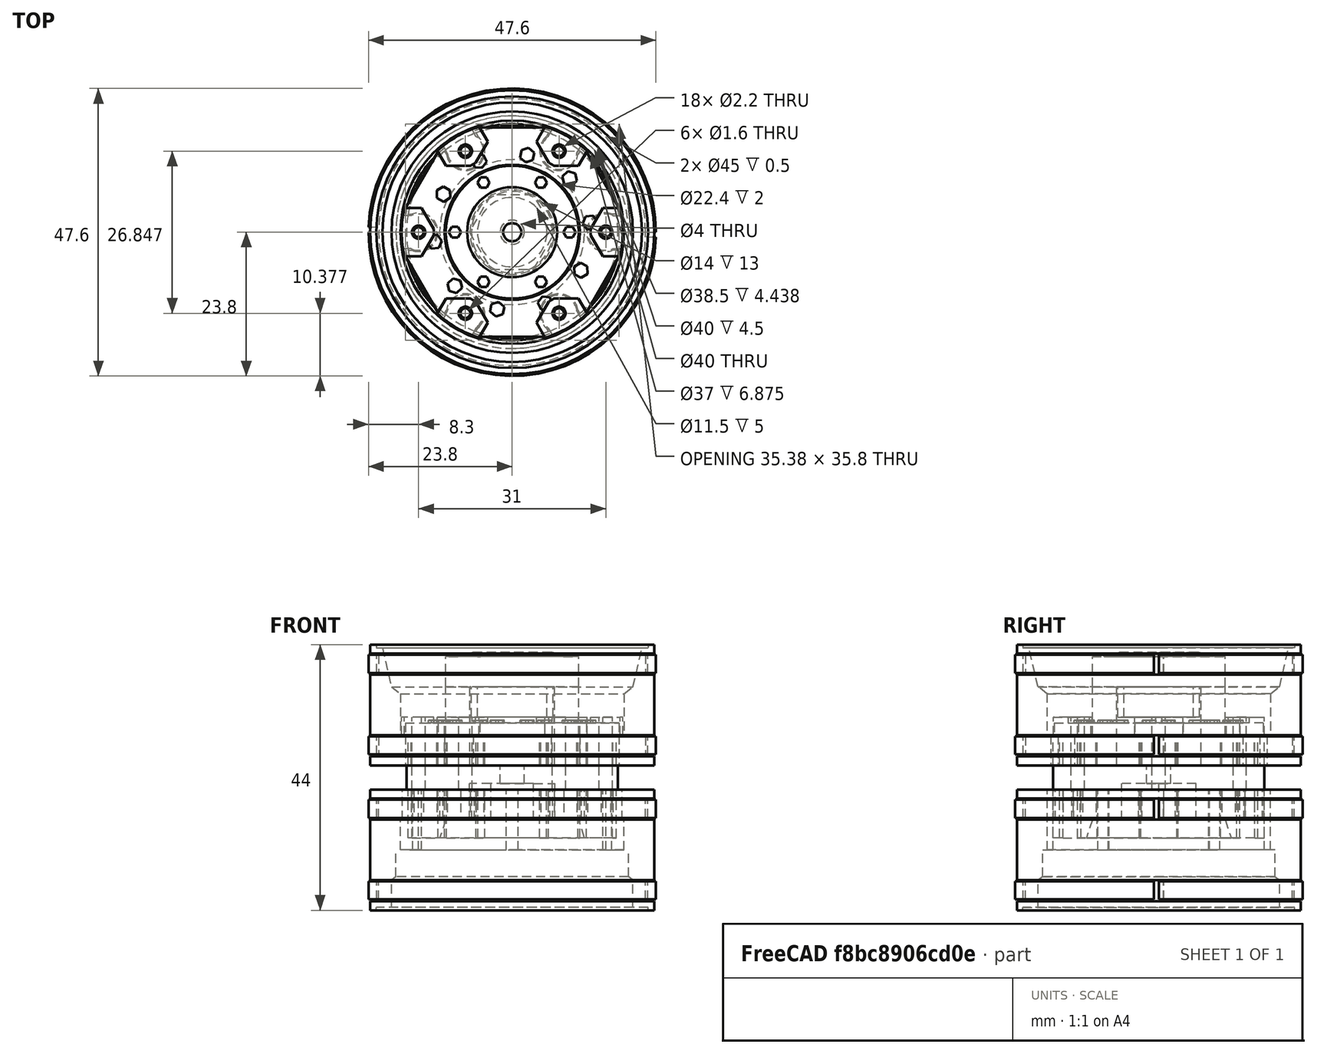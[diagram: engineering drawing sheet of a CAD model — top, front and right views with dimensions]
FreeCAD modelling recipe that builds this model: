
FCSTD DOCUMENT  (FreeCAD 0.18.4R)
Label: trilex_rear
License: All rights reserved
LicenseURL: http://en.wikipedia.org/wiki/All_rights_reserved
objects: Part::Cylinder×79, Part::MultiFuse×62, Part::Cut×43, Part::Box×17, Part::Feature×13, Part::Extrusion×5, Part::RegularPolygon×4, Part::Cone×3, Part::Fillet×2, Part::Chamfer×2
note: 230 computed .brp shape members not serialized (recipe doc carries the construction recipe); baked Part::Feature solids carry a one-line shape summary decoded from their .brp

FEATURE [Part::Cylinder] Cylinder
  Angle = 360
  AttacherType = Attacher::AttachEngine3D
  Height = 20
  Radius = 23.5
FEATURE [Part::Cylinder] Cylinder002
  Angle = 360
  AttacherType = Attacher::AttachEngine3D
  Height = 17
  Radius = 22.1
FEATURE [Part::Cylinder] Cylinder001
  Angle = 360
  AttacherType = Attacher::AttachEngine3D
  Height = 17
  Radius = 23.5
FEATURE [Part::Cut] Cut
  Base = -> Cylinder001
  Placement = pos=(0,0,1.5) rot=(0,0,1;0rad)
  Refine = true
  Tool = -> Cylinder002
FEATURE [Part::Cut] Cut001
  Base = -> Cylinder
  Refine = true
  Tool = -> Cut
FEATURE [Part::Cylinder] Cylinder003
  Angle = 360
  AttacherType = Attacher::AttachEngine3D
  Height = 17
  Radius = 22
FEATURE [Part::Cylinder] Cylinder004
  Angle = 360
  AttacherType = Attacher::AttachEngine3D
  Height = 10
  Placement = pos=(0,0,0.5) rot=(0,0,1;0rad)
  Radius = 23.5
FEATURE [Part::Cut] Cut002
  Base = -> Cylinder004
  Placement = pos=(0,0,4.5) rot=(0,0,1;0rad)
  Refine = true
  Tool = -> Cylinder003
FEATURE [Part::Cylinder] Cylinder006
  Angle = 360
  AttacherType = Attacher::AttachEngine3D
  Height = 20
  Radius = 18.5
FEATURE [Part::Cylinder] Cylinder007
  Angle = 360
  AttacherType = Attacher::AttachEngine3D
  Height = 5
  Placement = pos=(0,0,5) rot=(0,0,1;0rad)
  Radius = 19.25
FEATURE [Part::Cylinder] Cylinder018
  Angle = 360
  AttacherType = Attacher::AttachEngine3D
  Height = 0.5
  Radius = 22.5
FEATURE [Part::Cylinder] Cylinder070
  Angle = 360
  AttacherType = Attacher::AttachEngine3D
  Height = 5
  Radius = 20
FEATURE [Part::Cylinder] Cylinder071
  Angle = 360
  AttacherType = Attacher::AttachEngine3D
  Height = 10
  Placement = pos=(18.5,0,5) rot=(0,0,1;0rad)
  Radius = 1
FEATURE [Part::Cylinder] Cylinder072
  Angle = 360
  AttacherType = Attacher::AttachEngine3D
  Height = 10
  Placement = pos=(9.25,16.0215,5) rot=(0,0,1;1.0472rad)
  Radius = 1
FEATURE [Part::Cylinder] Cylinder073
  Angle = 360
  AttacherType = Attacher::AttachEngine3D
  Height = 10
  Placement = pos=(-9.25,16.0215,5) rot=(0,0,1;2.0944rad)
  Radius = 1
FEATURE [Part::Cylinder] Cylinder074
  Angle = 360
  AttacherType = Attacher::AttachEngine3D
  Height = 10
  Placement = pos=(-18.5,2e-15,5) rot=(0,0,1;3.14159rad)
  Radius = 1
FEATURE [Part::Cylinder] Cylinder075
  Angle = 360
  AttacherType = Attacher::AttachEngine3D
  Height = 10
  Placement = pos=(-9.25,-16.0215,5) rot=(0,0,1;4.18879rad)
  Radius = 1
FEATURE [Part::Cylinder] Cylinder076
  Angle = 360
  AttacherType = Attacher::AttachEngine3D
  Height = 10
  Placement = pos=(9.25,-16.0215,5) rot=(0,0,-1;1.0472rad)
  Radius = 1
FEATURE [Part::MultiFuse] Fusion030  label="rim-enforcement"
  Placement = pos=(0,0,-39) rot=(0,0,1;0.523599rad)
  Refine = true
  Shapes = -> [Cylinder071,Cylinder073,Cylinder075,Cylinder072,Cylinder074,Cylinder076]
FEATURE [Part::MultiFuse] Fusion
  Refine = true
  Shapes = -> [Cut002,Cut001]
FEATURE [Part::Cut] Cut031
  Base = -> Fusion
  Refine = true
  Tool = -> Cylinder006
FEATURE [Part::Cylinder] Cylinder078
  Angle = 178
  AttacherType = Attacher::AttachEngine3D
  Height = 3
  Placement = pos=(0,0,1.8) rot=(0,0,1;0rad)
  Radius = 23.8
FEATURE [Part::Cylinder] Cylinder079
  Angle = 360
  AttacherType = Attacher::AttachEngine3D
  Height = 17
  Radius = 22.45
FEATURE [Part::Cut] Cut035
  Base = -> Cylinder078
  Refine = true
  Tool = -> Cylinder079
FEATURE [Part::Cylinder] Cylinder080
  Angle = 178
  AttacherType = Attacher::AttachEngine3D
  Height = 3
  Placement = pos=(0,0,1.8) rot=(0,0,1;0rad)
  Radius = 23.8
FEATURE [Part::Cylinder] Cylinder081
  Angle = 360
  AttacherType = Attacher::AttachEngine3D
  Height = 17
  Radius = 22.45
FEATURE [Part::Cut] Cut036
  Base = -> Cylinder080
  Placement = pos=(0,0,0) rot=(0,0,1;3.14159rad)
  Refine = true
  Tool = -> Cylinder081
FEATURE [Part::MultiFuse] Fusion032
  Placement = pos=(0,0,13.5) rot=(0,0,1;0rad)
  Refine = true
  Shapes = -> [Cut035,Cut036]
FEATURE [Part::Cut] Cut037
  Base = -> Cylinder080
  Placement = pos=(0,0,0) rot=(0,0,1;3.14159rad)
  Refine = true
  Tool = -> Cylinder081
FEATURE [Part::Cut] Cut038
  Base = -> Cylinder078
  Refine = true
  Tool = -> Cylinder079
FEATURE [Part::MultiFuse] Fusion033
  Refine = true
  Shapes = -> [Cut038,Cut037]
FEATURE [Part::MultiFuse] Fusion034  label="trilex-rear-rim-inner-support"
  Placement = pos=(0,0,-44) rot=(0,0,1;0rad)
  Refine = true
  Shapes = -> [Fusion032,Fusion033]
FEATURE [Part::Cone] Cone
  Angle = 360
  AttacherType = Attacher::AttachEngine3D
  Height = 6
  Placement = pos=(0,0,5) rot=(0,0,1;0rad)
  Radius1 = 20
  Radius2 = 12
FEATURE [Part::Cut] Cut057
  Base = -> Cut031
  Refine = true
  Tool = -> Cylinder070
FEATURE [Part::Cut] Cut058
  Base = -> Cut057
  Refine = true
  Tool = -> Cylinder018
FEATURE [Part::Cut] Cut059
  Base = -> Cut058
  Refine = true
  Tool = -> Cone
FEATURE [Part::Cut] Cut060  label="rim-inner"
  Base = -> Cut059
  Placement = pos=(0,0,44) rot=(0,1,0;3.14159rad)
  Refine = true
  Tool = -> Cylinder007
FEATURE [Part::Cylinder] Cylinder098
  Angle = 360
  AttacherType = Attacher::AttachEngine3D
  Height = 5
  Placement = pos=(15.5,0,15) rot=(0,0,1;0rad)
  Radius = 0.8
FEATURE [Part::Cylinder] Cylinder100
  Angle = 360
  AttacherType = Attacher::AttachEngine3D
  Height = 5
  Placement = pos=(15.5,0,15) rot=(0,0,1;0rad)
  Radius = 3
FEATURE [Part::Box] Box012  label="Cube012"
  AttacherType = Attacher::AttachEngine3D
  Height = 5
  Length = 0.75
  Placement = pos=(18.2,-4,15) rot=(0,0,1;0rad)
  Width = 8
FEATURE [Part::Box] Box013  label="Cube013"
  AttacherType = Attacher::AttachEngine3D
  Height = 5
  Length = 2
  Placement = pos=(16.5,-2.75,15) rot=(0,0,1;0rad)
  Width = 5.5
FEATURE [Part::MultiFuse] Fusion042
  Refine = true
  Shapes = -> [Cylinder100,Box013,Box012]
FEATURE [Part::Cut] Cut063
  Base = -> Fusion042
  Placement = pos=(0,0,9) rot=(0,0,1;1.0472rad)
  Refine = true
  Tool = -> Cylinder098
FEATURE [Part::Cylinder] Cylinder101
  Angle = 360
  AttacherType = Attacher::AttachEngine3D
  Height = 5
  Placement = pos=(15.5,0,15) rot=(0,0,1;0rad)
  Radius = 0.8
FEATURE [Part::MultiFuse] Fusion043
  Refine = true
  Shapes = -> [Cylinder100,Box013,Box012]
FEATURE [Part::Cut] Cut064
  Base = -> Fusion043
  Placement = pos=(0,0,9) rot=(0,0,1;2.0944rad)
  Refine = true
  Tool = -> Cylinder101
FEATURE [Part::Cylinder] Cylinder102
  Angle = 360
  AttacherType = Attacher::AttachEngine3D
  Height = 5
  Placement = pos=(15.5,0,15) rot=(0,0,1;0rad)
  Radius = 0.8
FEATURE [Part::MultiFuse] Fusion044
  Refine = true
  Shapes = -> [Cylinder100,Box013,Box012]
FEATURE [Part::Cut] Cut065
  Base = -> Fusion044
  Placement = pos=(0,0,9) rot=(0,0,1;3.14159rad)
  Refine = true
  Tool = -> Cylinder102
FEATURE [Part::Cylinder] Cylinder103
  Angle = 360
  AttacherType = Attacher::AttachEngine3D
  Height = 5
  Placement = pos=(15.5,0,15) rot=(0,0,1;0rad)
  Radius = 0.8
FEATURE [Part::MultiFuse] Fusion045
  Refine = true
  Shapes = -> [Cylinder100,Box013,Box012]
FEATURE [Part::Cut] Cut066
  Base = -> Fusion045
  Placement = pos=(0,0,9) rot=(0,0,1;4.18879rad)
  Refine = true
  Tool = -> Cylinder103
FEATURE [Part::Cylinder] Cylinder104
  Angle = 360
  AttacherType = Attacher::AttachEngine3D
  Height = 5
  Placement = pos=(15.5,0,15) rot=(0,0,1;0rad)
  Radius = 0.8
FEATURE [Part::MultiFuse] Fusion046
  Refine = true
  Shapes = -> [Cylinder100,Box013,Box012]
FEATURE [Part::Cut] Cut067
  Base = -> Fusion046
  Placement = pos=(0,0,9) rot=(0,0,-1;1.0472rad)
  Refine = true
  Tool = -> Cylinder104
FEATURE [Part::Cylinder] Cylinder106
  Angle = 360
  AttacherType = Attacher::AttachEngine3D
  Height = 5
  Placement = pos=(15.5,0,15) rot=(0,0,1;0rad)
  Radius = 0.8
FEATURE [Part::MultiFuse] Fusion048
  Refine = true
  Shapes = -> [Cylinder100,Box013,Box012]
FEATURE [Part::Cut] Cut069
  Base = -> Fusion048
  Placement = pos=(0,0,9) rot=(0,0,1;0rad)
  Refine = true
  Tool = -> Cylinder106
FEATURE [Part::MultiFuse] Fusion049
  Refine = true
  Shapes = -> [Cut063,Cut064,Cut067,Cut065,Cut069,Cut066]
FEATURE [Part::MultiFuse] Fusion050  label="rim-inner-rear_"
  Placement = pos=(0,0,0) rot=(0,1,0;3.14159rad)
  Refine = true
  Shapes = -> [Cut060,Fusion049]
FEATURE [Part::Cylinder] Cylinder109
  Angle = 360
  AttacherType = Attacher::AttachEngine3D
  Height = 2
  Placement = pos=(0,0,-6) rot=(0,0,1;0rad)
  Radius = 7.5
FEATURE [Part::Fillet] Fillet059
  Base = -> Cylinder109
  Edges = 1 edges r=1: [Edge1]
  Placement = pos=(0,0,-6) rot=(0,0,1;0rad)
FEATURE [Part::Cylinder] Cylinder112
  Angle = 360
  AttacherType = Attacher::AttachEngine3D
  Height = 0.3
  Placement = pos=(0,0,-10.3) rot=(0,0,1;0rad)
  Radius = 1.5
FEATURE [Part::Cut] Cut072
  Base = -> Fillet059
  Refine = true
  Tool = -> Cylinder112
FEATURE [Part::Fillet] Fillet062
  Base = -> Cut072
  Edges = 1 edges r=0.29: [Edge6]
  Placement = pos=(0,0,8.7) rot=(0,0,1;0rad)
FEATURE [Part::Cylinder] Cylinder118
  Angle = 360
  AttacherType = Attacher::AttachEngine3D
  Height = 17
  Placement = pos=(0,0,-32) rot=(0,0,1;0rad)
  Radius = 17.5
FEATURE [Part::Cylinder] Cylinder119
  Angle = 360
  AttacherType = Attacher::AttachEngine3D
  Height = 8
  Placement = pos=(15.5,0,-29.5) rot=(0,0,1;0rad)
  Radius = 3.2
FEATURE [Part::Box] Box016  label="Cube016"
  AttacherType = Attacher::AttachEngine3D
  Height = 8
  Length = 3
  Placement = pos=(16,-3,-29.5) rot=(0,0,1;0rad)
  Width = 6
FEATURE [Part::MultiFuse] Fusion061
  Placement = pos=(0,0,0) rot=(0,0,1;1.0472rad)
  Refine = true
  Shapes = -> [Cylinder119,Box016]
FEATURE [Part::Cylinder] Cylinder120
  Angle = 360
  AttacherType = Attacher::AttachEngine3D
  Height = 8
  Placement = pos=(15.5,0,-29.5) rot=(0,0,1;0rad)
  Radius = 3.2
FEATURE [Part::Box] Box017  label="Cube017"
  AttacherType = Attacher::AttachEngine3D
  Height = 8
  Length = 3
  Placement = pos=(16,-3,-29.5) rot=(0,0,1;0rad)
  Width = 6
FEATURE [Part::MultiFuse] Fusion062
  Placement = pos=(0,0,0) rot=(0,0,1;2.0944rad)
  Refine = true
  Shapes = -> [Cylinder120,Box017]
FEATURE [Part::Cylinder] Cylinder121
  Angle = 360
  AttacherType = Attacher::AttachEngine3D
  Height = 8
  Placement = pos=(15.5,0,-29.5) rot=(0,0,1;0rad)
  Radius = 3.2
FEATURE [Part::Box] Box018  label="Cube018"
  AttacherType = Attacher::AttachEngine3D
  Height = 8
  Length = 3
  Placement = pos=(16,-3,-29.5) rot=(0,0,1;0rad)
  Width = 6
FEATURE [Part::MultiFuse] Fusion063
  Placement = pos=(0,0,0) rot=(0,0,1;3.14159rad)
  Refine = true
  Shapes = -> [Cylinder121,Box018]
FEATURE [Part::Cylinder] Cylinder122
  Angle = 360
  AttacherType = Attacher::AttachEngine3D
  Height = 8
  Placement = pos=(15.5,0,-29.5) rot=(0,0,1;0rad)
  Radius = 3.2
FEATURE [Part::Box] Box019  label="Cube019"
  AttacherType = Attacher::AttachEngine3D
  Height = 8
  Length = 3
  Placement = pos=(16,-3,-29.5) rot=(0,0,1;0rad)
  Width = 6
FEATURE [Part::MultiFuse] Fusion064
  Placement = pos=(0,0,0) rot=(0,0,1;4.18879rad)
  Refine = true
  Shapes = -> [Cylinder122,Box019]
FEATURE [Part::Cylinder] Cylinder123
  Angle = 360
  AttacherType = Attacher::AttachEngine3D
  Height = 8
  Placement = pos=(15.5,0,-29.5) rot=(0,0,1;0rad)
  Radius = 3.2
FEATURE [Part::Box] Box020  label="Cube020"
  AttacherType = Attacher::AttachEngine3D
  Height = 8
  Length = 3
  Placement = pos=(16,-3,-29.5) rot=(0,0,1;0rad)
  Width = 6
FEATURE [Part::MultiFuse] Fusion065
  Placement = pos=(0,0,0) rot=(0,0,-1;1.0472rad)
  Refine = true
  Shapes = -> [Cylinder123,Box020]
FEATURE [Part::Cylinder] Cylinder124
  Angle = 360
  AttacherType = Attacher::AttachEngine3D
  Height = 8
  Placement = pos=(15.5,0,-29.5) rot=(0,0,1;0rad)
  Radius = 3.2
FEATURE [Part::Box] Box021  label="Cube021"
  AttacherType = Attacher::AttachEngine3D
  Height = 8
  Length = 3
  Placement = pos=(16,-3,-29.5) rot=(0,0,1;0rad)
  Width = 6
FEATURE [Part::MultiFuse] Fusion066
  Refine = true
  Shapes = -> [Cylinder124,Box021]
FEATURE [Part::MultiFuse] Fusion067
  Placement = pos=(0,0,-2.5) rot=(0,0,1;0rad)
  Refine = true
  Shapes = -> [Fusion061,Fusion064,Fusion063,Fusion066,Fusion065,Fusion062]
FEATURE [Part::MultiFuse] Fusion070  label="trilex-rear-rim-inner"
  Refine = true
  Shapes = -> [Fusion030,Fusion050]
FEATURE [Part::Cylinder] Cylinder125
  Angle = 360
  AttacherType = Attacher::AttachEngine3D
  Height = 20
  Placement = pos=(0,0,-26.5) rot=(0,0,1;0rad)
  Radius = 2
FEATURE [Part::Cylinder] Cylinder126
  Angle = 360
  AttacherType = Attacher::AttachEngine3D
  Height = 14
  Placement = pos=(0,0,-20) rot=(0,0,1;0rad)
  Radius = 7
FEATURE [Part::MultiFuse] Fusion074
  Refine = true
  Shapes = -> [Cylinder126,Cylinder125]
FEATURE [Part::Feature] Face007
  shape: bbox 18.53 x 18.56 x 2e-07 mm, 1 faces, 0 solids (baked)
FEATURE [Part::Extrusion] Extrude007
  Base = -> Face007
  Dir = (0,0,6)
  DirMode = 0
  FaceMakerClass = Part::FaceMakerExtrusion
  LengthFwd = 0
  LengthRev = 0
  Placement = pos=(0,0,0.5) rot=(0,0,1;0rad)
  Solid = false
  Symmetric = false
FEATURE [Part::MultiFuse] Fusion078
  Refine = true
  Shapes = -> [Cut038,Cut037]
FEATURE [Part::MultiFuse] Fusion079
  Placement = pos=(0,0,13.5) rot=(0,0,1;0rad)
  Refine = true
  Shapes = -> [Cut035,Cut036]
FEATURE [Part::MultiFuse] Fusion077  label="trilex-rear-rim-outer-support"
  Placement = pos=(0,0,-20) rot=(0,0,1;0rad)
  Refine = true
  Shapes = -> [Fusion079,Fusion078]
FEATURE [Part::Cylinder] Cylinder130
  Angle = 360
  AttacherType = Attacher::AttachEngine3D
  Height = 5
  Placement = pos=(0,0,-7) rot=(0,0,1;0rad)
  Radius = 11
FEATURE [Part::Cylinder] Cylinder180
  Angle = 360
  AttacherType = Attacher::AttachEngine3D
  Height = 4
  Placement = pos=(-15.5,0,-24) rot=(0,0,1;0rad)
  Radius = 1.1
FEATURE [Part::Cylinder] Cylinder181
  Angle = 360
  AttacherType = Attacher::AttachEngine3D
  Height = 4
  Placement = pos=(-15.5,0,-24) rot=(0,0,1;0rad)
  Radius = 1.1
FEATURE [Part::Feature] Fusion082011001  label="Fusion082012"
  Placement = pos=(0,0,0) rot=(0,0,1;0.820305rad)
  shape: bbox 20.17 x 21.41 x 1 mm, 16 faces, 2 solids (baked)
FEATURE [Part::Feature] Chamfer001004  label="Chamfer005"
  Placement = pos=(0,0,0) rot=(0,0,1;4.18879rad)
  shape: bbox 8.928 x 7.464 x 3 mm, 8 faces (baked)
FEATURE [Part::Cylinder] Cylinder179
  Angle = 360
  AttacherType = Attacher::AttachEngine3D
  Height = 4
  Placement = pos=(15.5,0,-24) rot=(0,0,1;0rad)
  Radius = 1.1
FEATURE [Part::Feature] Fusion082011003  label="Fusion082014"
  Placement = pos=(0,0,0) rot=(0,0,1;2.07694rad)
  shape: bbox 15.1 x 24.93 x 1 mm, 16 faces, 2 solids (baked)
FEATURE [Part::Cylinder] Cylinder173
  Angle = 360
  AttacherType = Attacher::AttachEngine3D
  Height = 4
  Radius = 18.3
FEATURE [Part::Cylinder] Cylinder131
  Angle = 360
  AttacherType = Attacher::AttachEngine3D
  Height = 5
  Placement = pos=(0,0,-17) rot=(0,0,1;0rad)
  Radius = 6.75
FEATURE [Part::Cylinder] Cylinder132
  Angle = 360
  AttacherType = Attacher::AttachEngine3D
  Height = 5
  Placement = pos=(0,0,-17) rot=(0,0,1;0rad)
  Radius = 5.75
FEATURE [Part::Cut] Cut083
  Base = -> Cylinder131
  Placement = pos=(0,0,5) rot=(0,0,1;0rad)
  Refine = true
  Tool = -> Cylinder132
FEATURE [Part::Cylinder] Cylinder175
  Angle = 360
  AttacherType = Attacher::AttachEngine3D
  Height = 4
  Placement = pos=(0,0,-16) rot=(0,0,1;0rad)
  Radius = 11.2
FEATURE [Part::Cylinder] Cylinder170
  Angle = 360
  AttacherType = Attacher::AttachEngine3D
  Height = 4
  Placement = pos=(15.5,0,-24) rot=(0,0,1;0rad)
  Radius = 1.1
FEATURE [Part::MultiFuse] Fusion040020
  Refine = true
  Shapes = -> [Fusion074,Extrude007]
FEATURE [Part::Feature] Chamfer001003  label="Chamfer004"
  Placement = pos=(0,0,0) rot=(0,0,1;3.14159rad)
  shape: bbox 6 x 8 x 3 mm, 8 faces (baked)
FEATURE [Part::Feature] Chamfer001002  label="Chamfer003"
  Placement = pos=(0,0,0) rot=(0,0,1;2.0944rad)
  shape: bbox 8.928 x 7.464 x 3 mm, 8 faces (baked)
FEATURE [Part::Cylinder] Cylinder161
  Angle = 360
  AttacherType = Attacher::AttachEngine3D
  Height = 8
  Placement = pos=(15.5,0,-29.5) rot=(0,0,1;0rad)
  Radius = 3.2
FEATURE [Part::Cylinder] Cylinder143
  Angle = 360
  AttacherType = Attacher::AttachEngine3D
  Height = 7
  Placement = pos=(0,0,8) rot=(0,0,1;0rad)
  Radius = 18.5
FEATURE [Part::Cylinder] Cylinder166
  Angle = 360
  AttacherType = Attacher::AttachEngine3D
  Height = 4
  Placement = pos=(-15.5,0,-24) rot=(0,0,1;0rad)
  Radius = 1.1
FEATURE [Part::Feature] Fusion082011004  label="Fusion082015"
  Placement = pos=(0,0,0) rot=(0,0,1;2.70526rad)
  shape: bbox 25.83 x 13.48 x 1 mm, 16 faces, 2 solids (baked)
FEATURE [Part::Box] Box027  label="Cube027"
  AttacherType = Attacher::AttachEngine3D
  Height = 8
  Length = 3
  Placement = pos=(16,-3,-29.5) rot=(0,0,1;0rad)
  Width = 6
FEATURE [Part::Box] Box029  label="Cube029"
  AttacherType = Attacher::AttachEngine3D
  Height = 8
  Length = 3
  Placement = pos=(16,-3,-29.5) rot=(0,0,1;0rad)
  Width = 6
FEATURE [Part::Cylinder] Cylinder159
  Angle = 360
  AttacherType = Attacher::AttachEngine3D
  Height = 8
  Placement = pos=(15.5,0,-29.5) rot=(0,0,1;0rad)
  Radius = 3.2
FEATURE [Part::Cylinder] Cylinder160
  Angle = 360
  AttacherType = Attacher::AttachEngine3D
  Height = 8
  Placement = pos=(15.5,0,-29.5) rot=(0,0,1;0rad)
  Radius = 3.2
FEATURE [Part::Box] Box025  label="Cube025"
  AttacherType = Attacher::AttachEngine3D
  Height = 8
  Length = 3
  Placement = pos=(16,-3,-29.5) rot=(0,0,1;0rad)
  Width = 6
FEATURE [Part::Cylinder] Cylinder172
  Angle = 360
  AttacherType = Attacher::AttachEngine3D
  Height = 10
  Placement = pos=(0,0,-17) rot=(0,0,1;0rad)
  Radius = 7
FEATURE [Part::RegularPolygon] RegularPolygon  label="Regular polygon"
  AttacherType = Attacher::AttachEngine3D
  Circumradius = 20
  Polygon = 6
FEATURE [Part::Extrusion] Extrude008
  Base = -> RegularPolygon
  Dir = (0,0,1)
  DirMode = 0
  FaceMakerClass = Part::FaceMakerBullseye
  LengthFwd = 2
  LengthRev = 0
  Placement = pos=(0,0,-15) rot=(0,0,1;0rad)
  Solid = true
  Symmetric = false
FEATURE [Part::Cylinder] Cylinder174
  Angle = 360
  AttacherType = Attacher::AttachEngine3D
  Height = 4
  Radius = 21
FEATURE [Part::Cylinder] Cylinder178
  Angle = 360
  AttacherType = Attacher::AttachEngine3D
  Height = 4
  Placement = pos=(15.5,0,-24) rot=(0,0,1;0rad)
  Radius = 1.1
FEATURE [Part::Box] Box  label="Cube"
  AttacherType = Attacher::AttachEngine3D
  Height = 3
  Length = 6
  Placement = pos=(13,-4,-15) rot=(0,0,1;0rad)
  Width = 8
FEATURE [Part::Chamfer] Chamfer001
  Base = -> Box
  Edges = 2 edges: [Edge1 r1=3.5 r2=2,Edge3 r1=3.5 r2=2]
FEATURE [Part::Cone] Cone002
  Angle = 360
  AttacherType = Attacher::AttachEngine3D
  Height = 3
  Placement = pos=(0,0,-32) rot=(0,0,1;0rad)
  Radius1 = 12
  Radius2 = 11
FEATURE [Part::Cylinder] Cylinder139
  Angle = 360
  AttacherType = Attacher::AttachEngine3D
  Height = 17
  Radius = 23.5
FEATURE [Part::Cylinder] Cylinder138
  Angle = 360
  AttacherType = Attacher::AttachEngine3D
  Height = 17
  Radius = 22.1
FEATURE [Part::Cylinder] Cylinder177
  Angle = 360
  AttacherType = Attacher::AttachEngine3D
  Height = 4
  Placement = pos=(-15.5,0,-24) rot=(0,0,1;0rad)
  Radius = 1.1
FEATURE [Part::Cylinder] Cylinder176
  Angle = 360
  AttacherType = Attacher::AttachEngine3D
  Height = 4
  Placement = pos=(15.5,0,-24) rot=(0,0,1;0rad)
  Radius = 1.1
FEATURE [Part::Cylinder] Cylinder164
  Angle = 360
  AttacherType = Attacher::AttachEngine3D
  Height = 8
  Placement = pos=(15.5,0,-29.5) rot=(0,0,1;0rad)
  Radius = 3.2
FEATURE [Part::Cut] Cut033005
  Base = -> Cylinder139
  Placement = pos=(0,0,1.5) rot=(0,0,1;0rad)
  Refine = true
  Tool = -> Cylinder138
FEATURE [Part::Cylinder] Cylinder141
  Angle = 360
  AttacherType = Attacher::AttachEngine3D
  Height = 10
  Placement = pos=(0,0,0.5) rot=(0,0,1;0rad)
  Radius = 23.5
FEATURE [Part::Cylinder] Cylinder153
  Angle = 360
  AttacherType = Attacher::AttachEngine3D
  Height = 5
  Placement = pos=(15.5,0,15) rot=(0,0,1;0rad)
  Radius = 3
FEATURE [Part::MultiFuse] Fusion082006
  Placement = pos=(0,0,0) rot=(0,0,1;1.0472rad)
  Refine = true
  Shapes = -> [Cylinder181,Cylinder178]
FEATURE [Part::Cylinder] Cylinder140
  Angle = 360
  AttacherType = Attacher::AttachEngine3D
  Height = 17
  Radius = 22
FEATURE [Part::Cut] Cut033003
  Base = -> Cylinder141
  Placement = pos=(0,0,4.5) rot=(0,0,1;0rad)
  Refine = true
  Tool = -> Cylinder140
FEATURE [Part::Cut] Cut033023
  Base = -> Extrude008
  Refine = true
  Tool = -> Cylinder175
FEATURE [Part::Cylinder] Cylinder155
  Angle = 360
  AttacherType = Attacher::AttachEngine3D
  Height = 5
  Placement = pos=(15.5,0,15) rot=(0,0,1;0rad)
  Radius = 1.1
FEATURE [Part::Cylinder] Cylinder157
  Angle = 360
  AttacherType = Attacher::AttachEngine3D
  Height = 5
  Placement = pos=(15.5,0,15) rot=(0,0,1;0rad)
  Radius = 1.1
FEATURE [Part::Box] Box023  label="Cube023"
  AttacherType = Attacher::AttachEngine3D
  Height = 5
  Length = 0.75
  Placement = pos=(18.2,-4,15) rot=(0,0,1;0rad)
  Width = 8
FEATURE [Part::RegularPolygon] RegularPolygon002  label="Regular polygon002"
  AttacherType = Attacher::AttachEngine3D
  Circumradius = 1.25
  Polygon = 6
FEATURE [Part::RegularPolygon] RegularPolygon001  label="Regular polygon001"
  AttacherType = Attacher::AttachEngine3D
  Circumradius = 1.25
  Polygon = 6
FEATURE [Part::Extrusion] Extrude009
  Base = -> RegularPolygon001
  Dir = (0,0,1)
  DirMode = 0
  FaceMakerClass = Part::FaceMakerBullseye
  LengthFwd = 1
  LengthRev = 0
  Placement = pos=(13,0,-13.5) rot=(0,0,1;0rad)
  Solid = true
  Symmetric = false
FEATURE [Part::MultiFuse] Fusion040012
  Placement = pos=(0,0,0) rot=(0,0,1;1.0472rad)
  Refine = true
  Shapes = -> [Cylinder159,Box025]
FEATURE [Part::Cylinder] Cylinder163
  Angle = 360
  AttacherType = Attacher::AttachEngine3D
  Height = 8
  Placement = pos=(15.5,0,-29.5) rot=(0,0,1;0rad)
  Radius = 3.2
FEATURE [Part::Cylinder] Cylinder137
  Angle = 360
  AttacherType = Attacher::AttachEngine3D
  Height = 20
  Radius = 23.5
FEATURE [Part::Cut] Cut033004
  Base = -> Cylinder137
  Refine = true
  Tool = -> Cut033005
FEATURE [Part::MultiFuse] Fusion040003
  Refine = true
  Shapes = -> [Cut033003,Cut033004]
FEATURE [Part::MultiFuse] Fusion082002
  Refine = true
  Shapes = -> [Fillet062,Cylinder130]
FEATURE [Part::MultiFuse] Fusion082003
  Refine = true
  Shapes = -> [Cut083,Fusion082002]
FEATURE [Part::Cylinder] Cylinder154
  Angle = 360
  AttacherType = Attacher::AttachEngine3D
  Height = 5
  Placement = pos=(15.5,0,15) rot=(0,0,1;0rad)
  Radius = 1.1
FEATURE [Part::Cylinder] Cylinder142
  Angle = 360
  AttacherType = Attacher::AttachEngine3D
  Height = 20
  Radius = 17.9
FEATURE [Part::Cut] Cut033007
  Base = -> Fusion040003
  Refine = true
  Tool = -> Cylinder142
FEATURE [Part::Cylinder] Cylinder144
  Angle = 360
  AttacherType = Attacher::AttachEngine3D
  Height = 0.5
  Radius = 22.5
FEATURE [Part::Feature] Fusion082011002  label="Fusion082013"
  Placement = pos=(0,0,0) rot=(0,0,1;1.44862rad)
  shape: bbox 5.47 x 28.29 x 1 mm, 16 faces, 2 solids (baked)
FEATURE [Part::Cylinder] Cylinder168
  Angle = 360
  AttacherType = Attacher::AttachEngine3D
  Height = 4
  Placement = pos=(15.5,0,-24) rot=(0,0,1;0rad)
  Radius = 1.1
FEATURE [Part::Cylinder] Cylinder156
  Angle = 360
  AttacherType = Attacher::AttachEngine3D
  Height = 5
  Placement = pos=(15.5,0,15) rot=(0,0,1;0rad)
  Radius = 1.1
FEATURE [Part::Cylinder] Cylinder158
  Angle = 360
  AttacherType = Attacher::AttachEngine3D
  Height = 5
  Placement = pos=(15.5,0,15) rot=(0,0,1;0rad)
  Radius = 1.1
FEATURE [Part::Cylinder] Cylinder165
  Angle = 360
  AttacherType = Attacher::AttachEngine3D
  Height = 4
  Placement = pos=(15.5,0,-24) rot=(0,0,1;0rad)
  Radius = 1.1
FEATURE [Part::Cylinder] Cylinder152
  Angle = 360
  AttacherType = Attacher::AttachEngine3D
  Height = 5
  Placement = pos=(15.5,0,15) rot=(0,0,1;0rad)
  Radius = 1.1
FEATURE [Part::Cylinder] Cylinder162
  Angle = 360
  AttacherType = Attacher::AttachEngine3D
  Height = 8
  Placement = pos=(15.5,0,-29.5) rot=(0,0,1;0rad)
  Radius = 3.2
FEATURE [Part::Box] Box024  label="Cube024"
  AttacherType = Attacher::AttachEngine3D
  Height = 5
  Length = 2
  Placement = pos=(16.5,-2.75,15) rot=(0,0,1;0rad)
  Width = 5.5
FEATURE [Part::MultiFuse] Fusion040006
  Refine = true
  Shapes = -> [Cylinder153,Box024,Box023]
FEATURE [Part::Cut] Cut033014
  Base = -> Fusion040006
  Placement = pos=(0,0,9) rot=(0,0,1;3.14159rad)
  Refine = true
  Tool = -> Cylinder155
FEATURE [Part::MultiFuse] Fusion040005
  Refine = true
  Shapes = -> [Cylinder153,Box024,Box023]
FEATURE [Part::MultiFuse] Fusion040007
  Refine = true
  Shapes = -> [Cylinder153,Box024,Box023]
FEATURE [Part::Cut] Cut033013
  Base = -> Fusion040005
  Placement = pos=(0,0,9) rot=(0,0,1;2.0944rad)
  Refine = true
  Tool = -> Cylinder154
FEATURE [Part::MultiFuse] Fusion040004
  Refine = true
  Shapes = -> [Cylinder153,Box024,Box023]
FEATURE [Part::MultiFuse] Fusion040009
  Refine = true
  Shapes = -> [Cylinder153,Box024,Box023]
FEATURE [Part::Cut] Cut033006
  Base = -> Fusion040009
  Placement = pos=(0,0,9) rot=(0,0,1;0rad)
  Refine = true
  Tool = -> Cylinder158
FEATURE [Part::Cut] Cut033012
  Base = -> Fusion040004
  Placement = pos=(0,0,9) rot=(0,0,1;1.0472rad)
  Refine = true
  Tool = -> Cylinder152
FEATURE [Part::MultiFuse] Fusion040008
  Refine = true
  Shapes = -> [Cylinder153,Box024,Box023]
FEATURE [Part::Cut] Cut033016
  Base = -> Fusion040008
  Placement = pos=(0,0,9) rot=(0,0,-1;1.0472rad)
  Refine = true
  Tool = -> Cylinder157
FEATURE [Part::MultiFuse] Fusion040021
  Refine = true
  Shapes = -> [Cylinder166,Cylinder165]
FEATURE [Part::Cylinder] Cylinder145
  Angle = 360
  AttacherType = Attacher::AttachEngine3D
  Height = 7
  Radius = 20
FEATURE [Part::Cut] Cut033015
  Base = -> Fusion040007
  Placement = pos=(0,0,9) rot=(0,0,1;4.18879rad)
  Refine = true
  Tool = -> Cylinder156
FEATURE [Part::MultiFuse] Fusion040010
  Refine = true
  Shapes = -> [Cut033012,Cut033013,Cut033016,Cut033014,Cut033006,Cut033015]
FEATURE [Part::Cylinder] Cylinder171
  Angle = 360
  AttacherType = Attacher::AttachEngine3D
  Height = 9.5
  Placement = pos=(0,0,-16.5) rot=(0,0,1;0rad)
  Radius = 11
FEATURE [Part::Cut] Cut033009
  Base = -> Cut033007
  Refine = true
  Tool = -> Cylinder145
FEATURE [Part::Box] Box030  label="Cube030"
  AttacherType = Attacher::AttachEngine3D
  Height = 8
  Length = 3
  Placement = pos=(16,-3,-29.5) rot=(0,0,1;0rad)
  Width = 6
FEATURE [Part::MultiFuse] Fusion040017
  Refine = true
  Shapes = -> [Cylinder164,Box030]
FEATURE [Part::Cylinder] Cylinder169
  Angle = 360
  AttacherType = Attacher::AttachEngine3D
  Height = 4
  Placement = pos=(-15.5,0,-24) rot=(0,0,1;0rad)
  Radius = 1.1
FEATURE [Part::MultiFuse] Fusion040023
  Placement = pos=(0,0,0) rot=(0,0,1;2.0944rad)
  Refine = true
  Shapes = -> [Cylinder169,Cylinder170]
FEATURE [Part::Cut] Cut033008
  Base = -> Cut033009
  Refine = true
  Tool = -> Cylinder144
FEATURE [Part::Extrusion] Extrude010
  Base = -> RegularPolygon002
  Dir = (0,0,1)
  DirMode = 0
  FaceMakerClass = Part::FaceMakerBullseye
  LengthFwd = 1
  LengthRev = 0
  Placement = pos=(-13,0,-13.5) rot=(0,0,1;0rad)
  Solid = true
  Symmetric = false
FEATURE [Part::MultiFuse] Fusion082011
  Placement = pos=(0,0,0) rot=(0,0,1;0.191986rad)
  Refine = true
  Shapes = -> [Extrude010,Extrude009]
FEATURE [Part::MultiFuse] Fusion082011005
  Placement = pos=(0,0,0) rot=(0,0,1;0.558505rad)
  Refine = true
  Shapes = -> [Fusion082011,Fusion082011001,Fusion082011003,Fusion082011004,Fusion082011002]
FEATURE [Part::Cone] Cone001
  Angle = 360
  AttacherType = Attacher::AttachEngine3D
  Height = 6
  Placement = pos=(0,0,7) rot=(0,0,1;0rad)
  Radius1 = 20
  Radius2 = 12
FEATURE [Part::Cut] Cut033010
  Base = -> Cut033008
  Refine = true
  Tool = -> Cone001
FEATURE [Part::Cut] Cut033011  label="rim-inner001"
  Base = -> Cut033010
  Placement = pos=(0,0,44) rot=(0,1,0;3.14159rad)
  Refine = true
  Tool = -> Cylinder143
FEATURE [Part::MultiFuse] Fusion040011
  Placement = pos=(0,0,-44) rot=(0,1,0;0rad)
  Refine = true
  Shapes = -> [Cut033011,Fusion040010]
FEATURE [Part::Box] Box028  label="Cube028"
  AttacherType = Attacher::AttachEngine3D
  Height = 8
  Length = 3
  Placement = pos=(16,-3,-29.5) rot=(0,0,1;0rad)
  Width = 6
FEATURE [Part::MultiFuse] Fusion040015
  Placement = pos=(0,0,0) rot=(0,0,1;4.18879rad)
  Refine = true
  Shapes = -> [Cylinder162,Box028]
FEATURE [Part::MultiFuse] Fusion040014
  Placement = pos=(0,0,0) rot=(0,0,1;3.14159rad)
  Refine = true
  Shapes = -> [Cylinder161,Box027]
FEATURE [Part::MultiFuse] Fusion040016
  Placement = pos=(0,0,0) rot=(0,0,-1;1.0472rad)
  Refine = true
  Shapes = -> [Cylinder163,Box029]
FEATURE [Part::Chamfer] Chamfer  label="trilex-rear-rim-outer"
  Base = -> Fusion040011
  Edges = 1 edges: [Edge36 r1=1.5 r2=6.499]
FEATURE [Part::MultiFuse] Fusion082005
  Placement = pos=(0,0,0) rot=(0,0,1;2.0944rad)
  Refine = true
  Shapes = -> [Cylinder180,Cylinder176]
FEATURE [Part::Box] Box026  label="Cube026"
  AttacherType = Attacher::AttachEngine3D
  Height = 8
  Length = 3
  Placement = pos=(16,-3,-29.5) rot=(0,0,1;0rad)
  Width = 6
FEATURE [Part::MultiFuse] Fusion040013
  Placement = pos=(0,0,0) rot=(0,0,1;2.0944rad)
  Refine = true
  Shapes = -> [Cylinder160,Box026]
FEATURE [Part::MultiFuse] Fusion040018
  Placement = pos=(0,0,9.5) rot=(0,0,1;0rad)
  Refine = true
  Shapes = -> [Fusion040012,Fusion040015,Fusion040014,Fusion040017,Fusion040016,Fusion040013]
FEATURE [Part::MultiFuse] Fusion040019
  Refine = true
  Shapes = -> [Fusion040018,Fusion067]
FEATURE [Part::Cut] Cut033017
  Base = -> Cylinder118
  Refine = true
  Tool = -> Fusion040019
FEATURE [Part::Cut] Cut033018
  Base = -> Cut033017
  Refine = true
  Tool = -> Cone002
FEATURE [Part::Cylinder] Cylinder167
  Angle = 360
  AttacherType = Attacher::AttachEngine3D
  Height = 4
  Placement = pos=(-15.5,0,-24) rot=(0,0,1;0rad)
  Radius = 1.1
FEATURE [Part::MultiFuse] Fusion040022
  Placement = pos=(0,0,0) rot=(0,0,1;1.0472rad)
  Refine = true
  Shapes = -> [Cylinder167,Cylinder168]
FEATURE [Part::MultiFuse] Fusion040024
  Refine = true
  Shapes = -> [Fusion040021,Fusion040023,Fusion040022]
FEATURE [Part::Cut] Cut033019
  Base = -> Cut033018
  Refine = true
  Tool = -> Fusion040020
FEATURE [Part::Cut] Cut033020
  Base = -> Cut033019
  Refine = true
  Tool = -> Fusion040024
FEATURE [Part::Feature] Chamfer001001  label="Chamfer002"
  Placement = pos=(0,0,0) rot=(0,0,1;1.0472rad)
  shape: bbox 8.928 x 7.464 x 3 mm, 8 faces (baked)
FEATURE [Part::MultiFuse] Fusion082008
  Refine = true
  Shapes = -> [Cylinder177,Cylinder179]
FEATURE [Part::Cut] Cut033021
  Base = -> Cylinder171
  Refine = true
  Tool = -> Cylinder172
FEATURE [Part::MultiFuse] Fusion082004  label="trilex-rear-hub-inner"
  Refine = true
  Shapes = -> [Cut033020,Cut033021]
FEATURE [Part::MultiFuse] Fusion082007
  Placement = pos=(0,0,9) rot=(0,0,1;0rad)
  Refine = true
  Shapes = -> [Fusion082008,Fusion082005,Fusion082006]
FEATURE [Part::Cut] Cut033022
  Base = -> Cylinder174
  Placement = pos=(0,0,-15) rot=(0,0,1;0rad)
  Refine = true
  Tool = -> Cylinder173
FEATURE [Part::Feature] Chamfer001005  label="Chamfer006"
  Placement = pos=(0,0,0) rot=(0,0,-1;1.0472rad)
  shape: bbox 8.928 x 7.464 x 3 mm, 8 faces (baked)
FEATURE [Part::MultiFuse] Fusion082009
  Refine = true
  Shapes = -> [Chamfer001005,Chamfer001004,Chamfer001,Chamfer001003,Chamfer001002,Chamfer001001]
FEATURE [Part::MultiFuse] Fusion082010
  Refine = true
  Shapes = -> [Cut033023,Fusion082009]
FEATURE [Part::Cut] Cut033024
  Base = -> Fusion082010
  Refine = true
  Tool = -> Cut033022
FEATURE [Part::Cut] Cut033025
  Base = -> Cut033024
  Refine = true
  Tool = -> Fusion082007
FEATURE [Part::MultiFuse] Fusion082011006  label="trilex-rear-hub-outer"
  Refine = true
  Shapes = -> [Cut033025,Fusion082011005]
FEATURE [Part::RegularPolygon] RegularPolygon003  label="Regular polygon003"
  AttacherType = Attacher::AttachEngine3D
  Circumradius = 1
  Polygon = 6
FEATURE [Part::Extrusion] Extrude
  Base = -> RegularPolygon003
  Dir = (0,0,1)
  DirMode = 2
  FaceMakerClass = Part::FaceMakerBullseye
  LengthFwd = 1
  LengthRev = 0
  Placement = pos=(9.5,0,-2.5) rot=(0,0,1;0rad)
  Solid = true
  Symmetric = false
FEATURE [Part::Feature] Extrude011
  Placement = pos=(-9.5,0,-2.5) rot=(0,0,1;0rad)
  shape: bbox 2 x 1.732 x 1 mm, 8 faces (baked)
FEATURE [Part::MultiFuse] Fusion082011007
  Refine = true
  Shapes = -> [Extrude011,Extrude]
FEATURE [Part::Feature] Fusion082011007001  label="Fusion082011008"
  Placement = pos=(0,0,0) rot=(0,0,1;1.0472rad)
  shape: bbox 11.5 x 18.19 x 1 mm, 16 faces, 2 solids (baked)
FEATURE [Part::Feature] Fusion082011007002  label="Fusion082011009"
  Placement = pos=(0,0,0) rot=(0,0,1;2.0944rad)
  shape: bbox 11.5 x 18.19 x 1 mm, 16 faces, 2 solids (baked)
FEATURE [Part::MultiFuse] Fusion082011007003
  Refine = true
  Shapes = -> [Fusion082011007002,Fusion082011007,Fusion082011007001]
FEATURE [Part::MultiFuse] Fusion082011007004  label="trilex-rear-hub-cap"
  Refine = true
  Shapes = -> [Fusion082011007003,Fusion082003]
